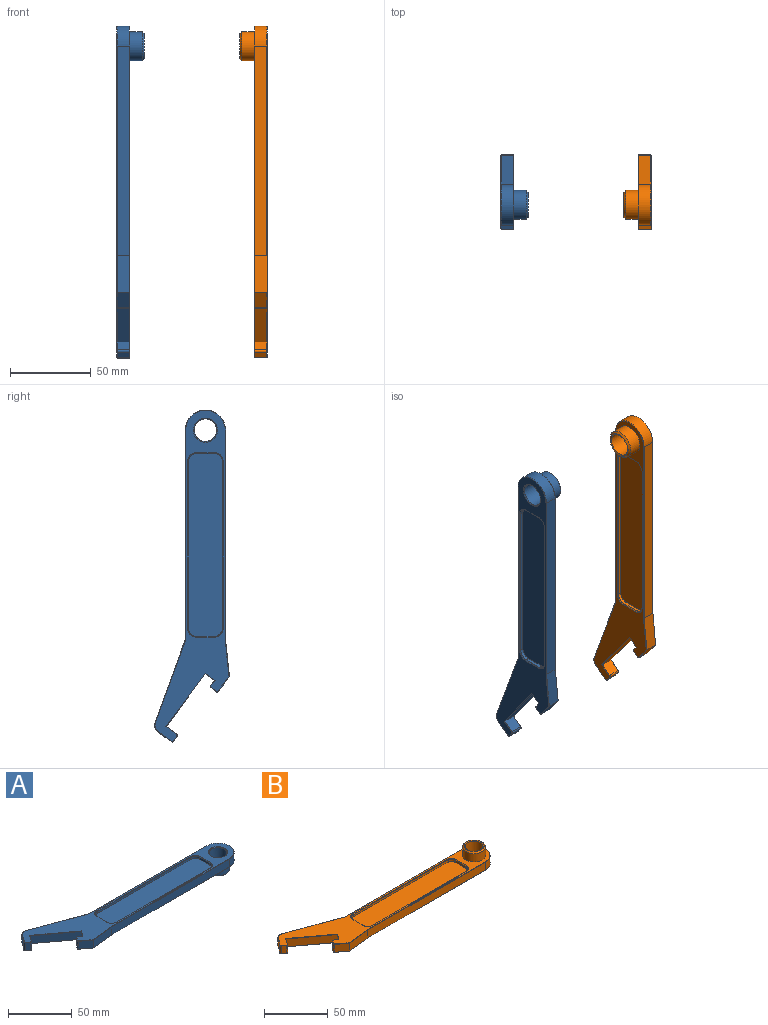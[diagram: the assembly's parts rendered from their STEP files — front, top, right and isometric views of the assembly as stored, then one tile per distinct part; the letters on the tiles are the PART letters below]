
ASSEMBLY  parts=2 mates=1
PART A: 97 faces, bbox 206x46.4x17.1 mm
  f0: plane 205.54x45.94mm, normal (0,0,1), area 1965.5mm2, adj f42,f43,f44,f45,f46,f47,f48,f49
  f1: plane 25.36x7.75mm, normal (0.1,-0.99,0), area 179.2mm2, adj f2,f13,f15,f60,f77,f95
  f2: plane 130x7.5mm, normal (0,-1,0), area 975mm2, adj f1,f3,f77,f93
  f3: cylinder r=12.5mm len=25mm, axis (0,0,-1), area 294.5mm2, adj f2,f4,f76,f91
  f4: plane 129.82x7.5mm, normal (0,1,0), area 973.7mm2, adj f3,f18,f75,f89
  f5: plane 51.34x18.69mm, normal (0.34,0.94,0), area 409.7mm2, adj f17,f18,f73,f85
  f6: plane 8.25x7.5mm, normal (-0.8,0.6,0), area 77mm2, adj f17,f19,f71,f81
  f7: plane 7.5x3.21mm, normal (-0.6,-0.8,0), area 30mm2, adj f19,f20,f69,f78
  f8: plane 7.5x6.43mm, normal (0.8,-0.6,0), area 60mm2, adj f9,f20,f67,f82
  f9: plane 32.53x24.13mm, normal (-0.6,-0.8,0), area 303.7mm2, adj f8,f10,f66,f84
  f10: plane 7.5x5.62mm, normal (-0.8,0.6,0), area 52.5mm2, adj f9,f11,f65,f86
  f11: plane 7.5x3.21mm, normal (0.6,0.8,0), area 30mm2, adj f10,f21,f64,f88
  f12: plane 7.5x3.21mm, normal (-0.8,0.6,0), area 30mm2, adj f21,f22,f62,f92
  f13: plane 9.22x7.5mm, normal (-0.6,-0.8,0), area 86.1mm2, adj f1,f22,f60,f96
  f14: cylinder r=7mm len=16.29mm, axis (0,0,-1), area 716.6mm2, adj f58,f59
  f15: plane 205.54x46.16mm, normal (0,0,-1), area 1893.8mm2, adj f1,f16,f50,f51,f52,f53,f54,f55
  f16: cylinder r=9mm len=18mm, axis (0,0,1), area 452.4mm2, adj f15,f41
  f17: cylinder r=5mm len=7.5mm, axis (0,0,-1), area 48.1mm2, adj f5,f6,f72,f83
  f18: cylinder r=1mm len=7.5mm, axis (0,0,1), area 2.6mm2, adj f4,f5,f74,f87
  f19: cylinder r=1mm len=7.5mm, axis (0,0,-1), area 11.8mm2, adj f6,f7,f70,f79
  f20: cylinder r=1mm len=7.5mm, axis (0,0,-1), area 11.8mm2, adj f7,f8,f68,f80
  f21: cylinder r=1mm len=7.5mm, axis (0,0,-1), area 11.8mm2, adj f11,f12,f63,f90
  f22: cylinder r=1mm len=7.5mm, axis (0,0,-1), area 11.8mm2, adj f12,f13,f61,f94
  f23: plane 103.5x2mm, normal (0,-1,0), area 207mm2, adj f27,f28,f31,f42
  f24: plane 11x2mm, normal (1,0,0), area 22mm2, adj f27,f28,f29,f45
  f25: plane 103.5x2mm, normal (0,1,0), area 207mm2, adj f27,f29,f30,f49
  f26: plane 11x2mm, normal (-1,0,0), area 22mm2, adj f27,f30,f31,f46
  f27: plane 113.5x21mm, normal (0,0,1), area 2362mm2, adj f23,f24,f25,f26,f28,f29,f30,f31
  f28: cylinder r=5mm len=5mm, axis (0,0,1), area 15.7mm2, adj f23,f24,f27,f43
  f29: cylinder r=5mm len=5mm, axis (0,0,-1), area 15.7mm2, adj f24,f25,f27,f47
  f30: cylinder r=5mm len=5mm, axis (0,0,1), area 15.7mm2, adj f25,f26,f27,f48
  f31: cylinder r=5mm len=5mm, axis (0,0,-1), area 15.7mm2, adj f23,f26,f27,f44
  f32: plane 11x2mm, normal (1,0,0), area 22mm2, adj f36,f37,f40,f53
  f33: plane 103.5x2mm, normal (0,1,0), area 207mm2, adj f36,f37,f38,f57
  f34: plane 11x2mm, normal (-1,0,0), area 22mm2, adj f36,f38,f39,f54
  f35: plane 103.5x2mm, normal (0,-1,0), area 207mm2, adj f36,f39,f40,f50
  f36: plane 113.5x21mm, normal (0,0,-1), area 2362mm2, adj f32,f33,f34,f35,f37,f38,f39,f40
  f37: cylinder r=5mm len=5mm, axis (0,0,-1), area 15.7mm2, adj f32,f33,f36,f55
  f38: cylinder r=5mm len=5mm, axis (0,0,1), area 15.7mm2, adj f33,f34,f36,f56
  f39: cylinder r=5mm len=5mm, axis (0,0,-1), area 15.7mm2, adj f34,f35,f36,f52
  f40: cylinder r=5mm len=5mm, axis (0,0,1), area 15.7mm2, adj f32,f35,f36,f51
  f41: cone r=9mm half-angle=45deg, axis (0,0,1), area 85.8mm2, adj f16,f58
  f42: plane 103.5x0.5mm, normal (0,-0.71,0.71), area 73.2mm2, adj f0,f23,f43,f44
  f43: cone r=5.5mm half-angle=45deg, axis (0,0,1), area 5.8mm2, adj f0,f28,f42,f45
  f44: cone r=5.5mm half-angle=45deg, axis (0,0,1), area 5.8mm2, adj f0,f31,f42,f46
  f45: plane 11x0.5mm, normal (0.71,0,0.71), area 7.8mm2, adj f0,f24,f43,f47
  f46: plane 11x0.5mm, normal (-0.71,0,0.71), area 7.8mm2, adj f0,f26,f44,f48
  f47: cone r=5.5mm half-angle=45deg, axis (0,0,1), area 5.8mm2, adj f0,f29,f45,f49
  f48: cone r=5.5mm half-angle=45deg, axis (0,0,1), area 5.8mm2, adj f0,f30,f46,f49
  f49: plane 103.5x0.5mm, normal (0,0.71,0.71), area 73.2mm2, adj f0,f25,f47,f48
  f50: plane 103.5x0.5mm, normal (0,-0.71,-0.71), area 73.2mm2, adj f15,f35,f51,f52
  f51: cone r=5.5mm half-angle=45deg, axis (0,0,-1), area 5.8mm2, adj f15,f40,f50,f53
  f52: cone r=5.5mm half-angle=45deg, axis (0,0,-1), area 5.8mm2, adj f15,f39,f50,f54
  f53: plane 11x0.5mm, normal (0.71,0,-0.71), area 7.8mm2, adj f15,f32,f51,f55
  f54: plane 11x0.5mm, normal (-0.71,0,-0.71), area 7.8mm2, adj f15,f34,f52,f56
  f55: cone r=5.5mm half-angle=45deg, axis (0,0,-1), area 5.8mm2, adj f15,f37,f53,f57
  f56: cone r=5.5mm half-angle=45deg, axis (0,0,-1), area 5.8mm2, adj f15,f38,f54,f57
  f57: plane 103.5x0.5mm, normal (0,0.71,-0.71), area 73.2mm2, adj f15,f33,f55,f56
  f58: cone r=7.85mm half-angle=67.5deg, axis (0,0,-1), area 43.1mm2, adj f14,f41
  f59: cone r=7mm half-angle=45deg, axis (0,0,1), area 32.2mm2, adj f0,f14
  f60: plane 9.59x7.04mm, normal (-0.42,-0.57,-0.71), area 4.1mm2, adj f1,f13,f15,f61
  f61: cone r=0.75mm half-angle=45deg, axis (0,0,1), area 0.5mm2, adj f15,f22,f60,f62
  f62: plane 3.36x2.58mm, normal (-0.57,0.42,-0.71), area 1.4mm2, adj f12,f15,f61,f63
  f63: cone r=0.75mm half-angle=45deg, axis (0,0,1), area 0.5mm2, adj f15,f21,f62,f64
  f64: plane 3.41x2.73mm, normal (0.42,0.57,-0.71), area 1.5mm2, adj f11,f15,f63,f65
  f65: plane 6.02x4.52mm, normal (-0.57,0.42,-0.71), area 2.6mm2, adj f10,f15,f64,f66
  f66: plane 32.93x24.48mm, normal (-0.42,-0.57,-0.71), area 14.4mm2, adj f9,f15,f65,f67
  f67: plane 6.78x4.97mm, normal (0.57,-0.42,-0.71), area 2.9mm2, adj f8,f15,f66,f68
  f68: cone r=0.75mm half-angle=45deg, axis (0,0,1), area 0.5mm2, adj f15,f20,f67,f69
  f69: plane 3.36x2.58mm, normal (-0.42,-0.57,-0.71), area 1.4mm2, adj f7,f15,f68,f70
  f70: cone r=0.75mm half-angle=45deg, axis (0,0,1), area 0.5mm2, adj f15,f19,f69,f71
  f71: plane 8.4x6.32mm, normal (-0.57,0.42,-0.71), area 3.6mm2, adj f6,f15,f70,f72
  f72: cone r=4.75mm half-angle=45deg, axis (0,0,1), area 2.2mm2, adj f15,f17,f71,f73
  f73: plane 51.42x18.92mm, normal (0.24,0.66,-0.71), area 19.3mm2, adj f5,f15,f72,f74
  f74: cone r=1.25mm half-angle=45deg, axis (0,0,-1), area 0.1mm2, adj f15,f18,f73,f75
  f75: plane 129.82x0.25mm, normal (0,0.71,-0.71), area 45.9mm2, adj f4,f15,f74,f76
  f76: cone r=12.5mm half-angle=45deg, axis (0,0,1), area 13.7mm2, adj f3,f15,f75,f77
  f77: plane 130x0.25mm, normal (0,-0.71,-0.71), area 45.5mm2, adj f1,f2,f15,f76
  f78: plane 3.36x2.58mm, normal (-0.42,-0.57,0.71), area 1.4mm2, adj f0,f7,f79,f80
  f79: cone r=0.75mm half-angle=45deg, axis (0,0,-1), area 0.5mm2, adj f0,f19,f78,f81
  f80: cone r=0.75mm half-angle=45deg, axis (0,0,-1), area 0.5mm2, adj f0,f20,f78,f82
  f81: plane 8.4x6.32mm, normal (-0.57,0.42,0.71), area 3.6mm2, adj f0,f6,f79,f83
  f82: plane 6.78x4.97mm, normal (0.57,-0.42,0.71), area 2.9mm2, adj f0,f8,f80,f84
  f83: cone r=4.75mm half-angle=45deg, axis (0,0,-1), area 2.2mm2, adj f0,f17,f81,f85
  f84: plane 32.93x24.48mm, normal (-0.42,-0.57,0.71), area 14.4mm2, adj f0,f9,f82,f86
  f85: plane 51.42x18.92mm, normal (0.24,0.66,0.71), area 19.3mm2, adj f0,f5,f83,f87
  f86: plane 6.02x4.52mm, normal (-0.57,0.42,0.71), area 2.6mm2, adj f0,f10,f84,f88
  f87: cone r=1.25mm half-angle=45deg, axis (0,0,1), area 0.1mm2, adj f0,f18,f85,f89
  f88: plane 3.41x2.73mm, normal (0.42,0.57,0.71), area 1.5mm2, adj f0,f11,f86,f90
  f89: plane 129.82x0.25mm, normal (0,0.71,0.71), area 45.9mm2, adj f0,f4,f87,f91
  f90: cone r=0.75mm half-angle=45deg, axis (0,0,-1), area 0.5mm2, adj f0,f21,f88,f92
  f91: cone r=12.25mm half-angle=45deg, axis (0,0,-1), area 13.7mm2, adj f0,f3,f89,f93
  f92: plane 3.36x2.58mm, normal (-0.57,0.42,0.71), area 1.4mm2, adj f0,f12,f90,f94
  f93: plane 130.01x0.25mm, normal (0,-0.71,0.71), area 46mm2, adj f0,f2,f91,f95
  f94: cone r=0.75mm half-angle=45deg, axis (0,0,-1), area 0.5mm2, adj f0,f22,f92,f96
  f95: plane 22.97x2.65mm, normal (0.07,-0.7,0.71), area 8.2mm2, adj f0,f1,f93,f96
  f96: plane 9.29x7.04mm, normal (-0.42,-0.57,0.71), area 4mm2, adj f0,f13,f94,f95
PART B: 96 faces, bbox 206x46.4x17.1 mm
  f0: plane 205.54x45.94mm, normal (0,0,1), area 1887.8mm2, adj f16,f42,f43,f44,f45,f46,f47,f48
  f1: plane 25.36x7.75mm, normal (0.1,-0.99,0), area 179.2mm2, adj f2,f13,f15,f59,f76,f94
  f2: plane 130x7.5mm, normal (0,-1,0), area 975mm2, adj f1,f3,f76,f92
  f3: cylinder r=12.5mm len=25mm, axis (0,0,-1), area 294.5mm2, adj f2,f4,f75,f90
  f4: plane 129.82x7.5mm, normal (0,1,0), area 973.7mm2, adj f3,f18,f74,f88
  f5: plane 51.34x18.69mm, normal (0.34,0.94,0), area 409.7mm2, adj f17,f18,f72,f84
  f6: plane 8.25x7.5mm, normal (-0.8,0.6,0), area 77mm2, adj f17,f19,f70,f80
  f7: plane 7.5x3.21mm, normal (-0.6,-0.8,0), area 30mm2, adj f19,f20,f68,f77
  f8: plane 7.5x6.43mm, normal (0.8,-0.6,0), area 60mm2, adj f9,f20,f66,f81
  f9: plane 32.53x24.13mm, normal (-0.6,-0.8,0), area 303.7mm2, adj f8,f10,f65,f83
  f10: plane 7.5x5.62mm, normal (-0.8,0.6,0), area 52.5mm2, adj f9,f11,f64,f85
  f11: plane 7.5x3.21mm, normal (0.6,0.8,0), area 30mm2, adj f10,f21,f63,f87
  f12: plane 7.5x3.21mm, normal (-0.8,0.6,0), area 30mm2, adj f21,f22,f61,f91
  f13: plane 9.22x7.5mm, normal (-0.6,-0.8,0), area 86.1mm2, adj f1,f22,f59,f95
  f14: cylinder r=7mm len=16.79mm, axis (0,0,-1), area 738.6mm2, adj f15,f58
  f15: plane 205.54x46.16mm, normal (0,0,-1), area 1994.3mm2, adj f1,f14,f50,f51,f52,f53,f54,f55
  f16: cylinder r=9mm len=18mm, axis (0,0,-1), area 452.4mm2, adj f0,f41
  f17: cylinder r=5mm len=7.5mm, axis (0,0,-1), area 48.1mm2, adj f5,f6,f71,f82
  f18: cylinder r=1mm len=7.5mm, axis (0,0,1), area 2.6mm2, adj f4,f5,f73,f86
  f19: cylinder r=1mm len=7.5mm, axis (0,0,-1), area 11.8mm2, adj f6,f7,f69,f78
  f20: cylinder r=1mm len=7.5mm, axis (0,0,-1), area 11.8mm2, adj f7,f8,f67,f79
  f21: cylinder r=1mm len=7.5mm, axis (0,0,-1), area 11.8mm2, adj f11,f12,f62,f89
  f22: cylinder r=1mm len=7.5mm, axis (0,0,-1), area 11.8mm2, adj f12,f13,f60,f93
  f23: plane 103.5x2mm, normal (0,-1,0), area 207mm2, adj f27,f28,f31,f42
  f24: plane 11x2mm, normal (1,0,0), area 22mm2, adj f27,f28,f29,f45
  f25: plane 103.5x2mm, normal (0,1,0), area 207mm2, adj f27,f29,f30,f49
  f26: plane 11x2mm, normal (-1,0,0), area 22mm2, adj f27,f30,f31,f46
  f27: plane 113.5x21mm, normal (0,0,1), area 2362mm2, adj f23,f24,f25,f26,f28,f29,f30,f31
  f28: cylinder r=5mm len=5mm, axis (0,0,1), area 15.7mm2, adj f23,f24,f27,f43
  f29: cylinder r=5mm len=5mm, axis (0,0,-1), area 15.7mm2, adj f24,f25,f27,f47
  f30: cylinder r=5mm len=5mm, axis (0,0,1), area 15.7mm2, adj f25,f26,f27,f48
  f31: cylinder r=5mm len=5mm, axis (0,0,-1), area 15.7mm2, adj f23,f26,f27,f44
  f32: plane 11x2mm, normal (1,0,0), area 22mm2, adj f36,f37,f40,f53
  f33: plane 103.5x2mm, normal (0,1,0), area 207mm2, adj f36,f37,f38,f57
  f34: plane 11x2mm, normal (-1,0,0), area 22mm2, adj f36,f38,f39,f54
  f35: plane 103.5x2mm, normal (0,-1,0), area 207mm2, adj f36,f39,f40,f50
  f36: plane 113.5x21mm, normal (0,0,-1), area 2362mm2, adj f32,f33,f34,f35,f37,f38,f39,f40
  f37: cylinder r=5mm len=5mm, axis (0,0,-1), area 15.7mm2, adj f32,f33,f36,f55
  f38: cylinder r=5mm len=5mm, axis (0,0,1), area 15.7mm2, adj f33,f34,f36,f56
  f39: cylinder r=5mm len=5mm, axis (0,0,-1), area 15.7mm2, adj f34,f35,f36,f52
  f40: cylinder r=5mm len=5mm, axis (0,0,1), area 15.7mm2, adj f32,f35,f36,f51
  f41: cone r=7mm half-angle=45deg, axis (0,0,-1), area 85.8mm2, adj f16,f58
  f42: plane 103.5x0.5mm, normal (0,-0.71,0.71), area 73.2mm2, adj f0,f23,f43,f44
  f43: cone r=5.5mm half-angle=45deg, axis (0,0,1), area 5.8mm2, adj f0,f28,f42,f45
  f44: cone r=5.5mm half-angle=45deg, axis (0,0,1), area 5.8mm2, adj f0,f31,f42,f46
  f45: plane 11x0.5mm, normal (0.71,0,0.71), area 7.8mm2, adj f0,f24,f43,f47
  f46: plane 11x0.5mm, normal (-0.71,0,0.71), area 7.8mm2, adj f0,f26,f44,f48
  f47: cone r=5.5mm half-angle=45deg, axis (0,0,1), area 5.8mm2, adj f0,f29,f45,f49
  f48: cone r=5.5mm half-angle=45deg, axis (0,0,1), area 5.8mm2, adj f0,f30,f46,f49
  f49: plane 103.5x0.5mm, normal (0,0.71,0.71), area 73.2mm2, adj f0,f25,f47,f48
  f50: plane 103.5x0.5mm, normal (0,-0.71,-0.71), area 73.2mm2, adj f15,f35,f51,f52
  f51: cone r=5.5mm half-angle=45deg, axis (0,0,-1), area 5.8mm2, adj f15,f40,f50,f53
  f52: cone r=5.5mm half-angle=45deg, axis (0,0,-1), area 5.8mm2, adj f15,f39,f50,f54
  f53: plane 11x0.5mm, normal (0.71,0,-0.71), area 7.8mm2, adj f15,f32,f51,f55
  f54: plane 11x0.5mm, normal (-0.71,0,-0.71), area 7.8mm2, adj f15,f34,f52,f56
  f55: cone r=5.5mm half-angle=45deg, axis (0,0,-1), area 5.8mm2, adj f15,f37,f53,f57
  f56: cone r=5.5mm half-angle=45deg, axis (0,0,-1), area 5.8mm2, adj f15,f38,f54,f57
  f57: plane 103.5x0.5mm, normal (0,0.71,-0.71), area 73.2mm2, adj f15,f33,f55,f56
  f58: cone r=7mm half-angle=67.5deg, axis (0,0,1), area 43.1mm2, adj f14,f41
  f59: plane 9.59x7.04mm, normal (-0.42,-0.57,-0.71), area 4.1mm2, adj f1,f13,f15,f60
  f60: cone r=0.75mm half-angle=45deg, axis (0,0,1), area 0.5mm2, adj f15,f22,f59,f61
  f61: plane 3.36x2.58mm, normal (-0.57,0.42,-0.71), area 1.4mm2, adj f12,f15,f60,f62
  f62: cone r=0.75mm half-angle=45deg, axis (0,0,1), area 0.5mm2, adj f15,f21,f61,f63
  f63: plane 3.41x2.73mm, normal (0.42,0.57,-0.71), area 1.5mm2, adj f11,f15,f62,f64
  f64: plane 6.02x4.52mm, normal (-0.57,0.42,-0.71), area 2.6mm2, adj f10,f15,f63,f65
  f65: plane 32.93x24.48mm, normal (-0.42,-0.57,-0.71), area 14.4mm2, adj f9,f15,f64,f66
  f66: plane 6.78x4.97mm, normal (0.57,-0.42,-0.71), area 2.9mm2, adj f8,f15,f65,f67
  f67: cone r=0.75mm half-angle=45deg, axis (0,0,1), area 0.5mm2, adj f15,f20,f66,f68
  f68: plane 3.36x2.58mm, normal (-0.42,-0.57,-0.71), area 1.4mm2, adj f7,f15,f67,f69
  f69: cone r=0.75mm half-angle=45deg, axis (0,0,1), area 0.5mm2, adj f15,f19,f68,f70
  f70: plane 8.4x6.32mm, normal (-0.57,0.42,-0.71), area 3.6mm2, adj f6,f15,f69,f71
  f71: cone r=4.75mm half-angle=45deg, axis (0,0,1), area 2.2mm2, adj f15,f17,f70,f72
  f72: plane 51.42x18.92mm, normal (0.24,0.66,-0.71), area 19.3mm2, adj f5,f15,f71,f73
  f73: cone r=1.25mm half-angle=45deg, axis (0,0,-1), area 0.1mm2, adj f15,f18,f72,f74
  f74: plane 129.82x0.25mm, normal (0,0.71,-0.71), area 45.9mm2, adj f4,f15,f73,f75
  f75: cone r=12.5mm half-angle=45deg, axis (0,0,1), area 13.7mm2, adj f3,f15,f74,f76
  f76: plane 130x0.25mm, normal (0,-0.71,-0.71), area 45.5mm2, adj f1,f2,f15,f75
  f77: plane 3.36x2.58mm, normal (-0.42,-0.57,0.71), area 1.4mm2, adj f0,f7,f78,f79
  f78: cone r=0.75mm half-angle=45deg, axis (0,0,-1), area 0.5mm2, adj f0,f19,f77,f80
  f79: cone r=0.75mm half-angle=45deg, axis (0,0,-1), area 0.5mm2, adj f0,f20,f77,f81
  f80: plane 8.4x6.32mm, normal (-0.57,0.42,0.71), area 3.6mm2, adj f0,f6,f78,f82
  f81: plane 6.78x4.97mm, normal (0.57,-0.42,0.71), area 2.9mm2, adj f0,f8,f79,f83
  f82: cone r=4.75mm half-angle=45deg, axis (0,0,-1), area 2.2mm2, adj f0,f17,f80,f84
  f83: plane 32.93x24.48mm, normal (-0.42,-0.57,0.71), area 14.4mm2, adj f0,f9,f81,f85
  f84: plane 51.42x18.92mm, normal (0.24,0.66,0.71), area 19.3mm2, adj f0,f5,f82,f86
  f85: plane 6.02x4.52mm, normal (-0.57,0.42,0.71), area 2.6mm2, adj f0,f10,f83,f87
  f86: cone r=1.25mm half-angle=45deg, axis (0,0,1), area 0.1mm2, adj f0,f18,f84,f88
  f87: plane 3.41x2.73mm, normal (0.42,0.57,0.71), area 1.5mm2, adj f0,f11,f85,f89
  f88: plane 129.82x0.25mm, normal (0,0.71,0.71), area 45.9mm2, adj f0,f4,f86,f90
  f89: cone r=0.75mm half-angle=45deg, axis (0,0,-1), area 0.5mm2, adj f0,f21,f87,f91
  f90: cone r=12.25mm half-angle=45deg, axis (0,0,-1), area 13.7mm2, adj f0,f3,f88,f92
  f91: plane 3.36x2.58mm, normal (-0.57,0.42,0.71), area 1.4mm2, adj f0,f12,f89,f93
  f92: plane 130.01x0.25mm, normal (0,-0.71,0.71), area 46mm2, adj f0,f2,f90,f94
  f93: cone r=0.75mm half-angle=45deg, axis (0,0,-1), area 0.5mm2, adj f0,f22,f91,f95
  f94: plane 22.97x2.65mm, normal (0.07,-0.7,0.71), area 8.2mm2, adj f0,f1,f92,f95
  f95: plane 9.29x7.04mm, normal (-0.42,-0.57,0.71), area 4mm2, adj f0,f13,f93,f94
PLACE A rot(axis=(0,-1,0),90deg) t=(-189.52,-50.98,124.5)mm
PLACE B rot(axis=(0,-1,0),90deg) t=(-103.94,-50.98,124.5)mm
MATE fastened A.f14 <-> B.f14  axis (1,0,0) through (-180.73,-50.98,124.5)mm
